# Revit family: WCPan-FloorMounted-65cm-(SpecialNeeds)-Vitra-ConformaSeries_5817B003-0087
name_source: partatom
category: Plumbing Fixtures
revit_build: Autodesk Revit 2017 (Build: 20160225_1515(x64)
units: mm (PartAtom-declared; Revit-internal decimal feet)

## family parameters
Cut with Voids When Loaded = No
Host = Face
OmniClass Number = 23.45.05.21.11
OmniClass Title = Water Closets
Part Type = Normal
Room Calculation Point = No
Round Connector Dimension = Use Diameter
Shared = Yes

## types (2) — shared parameters
BIMobject category = Sanitary - Toilets
CW Connection = Yes
Color = White
Default Elevation = 450 mm  [stored 1.47638 ft]
Description = VitrA Conforma Special Needs Wc Pan
Design country = Turkey
HW Connection = No
IFC Classification = Sanitary Terminal
Main Material = Ceramic
Manufacturer = Vitra
Manufacturer name = Vitra
Masterformat 2014 Code = 22 45 26
Masterformat 2014 Description = Sanitary Facilities
MountingType = Floor Mounted
NBS Referans Code = 35-65-90
NBS Referans Description = Toilet Systems
Nominal Depth (mm) = 650 mm  [stored 2.13255 ft]
Nominal Height (mm) = 450 mm  [stored 1.47638 ft]
Nominal Width (mm) = 355 mm
OmniClass Code = 23-31 19 00
OmniClass Description = Toilets
Product certification = https://vitraglobal.com
Product data url = https://www.vitra.co.uk
Product family = Conforma
Product group = Special Needs Wc Pan
Secondary Material = Ceramic-White
Technical description = https://www.vitra.co.uk
UNSPSC Code = 301815
UNSPSC Description = Sanitary Ware
URL = https://www.vitra.com.tr
Uniclass 1.4 Code = L7216
Uniclass 1.4 Description = Toilets
Uniclass 2.0 Code = SS-35-65-90
Uniclass 2.0 Description = Toilet Systems
Uniclass 2015 Code = Pr_40_20_93
Uniclass 2015 Name = Urinal and WC fittings
Uniformat II Code = D2010
Uniformat II Description = Sanitary Facilities
Vent Connection = No
Warranty Period (Year) = 10 Years
Waste Connection = Yes
Weight Net (kg) = 36,741
Youtube = https://www.youtube.com
zero-valued in all types: Cost

## per-type parameters (varying)
| type | Article No. (default) | Model | Product SKU |
| WCPan-FloorMounted-65cm-(SpecialNeeds)-Vitra-ConformaSeries_5817B003-0087 | 5817B003-0087 | 5817B003-0087 | 5817B003-0087 |
| WCPan-FloorMounted-65cm-(SpecialNeeds)-Vitra-ConformaSeries_5817B003-7700 | 5817B003-7700 | 5817B003-7700 | 5817B003-7700 |

note: [stored X ft] marks values corroborated as IEEE doubles in the binary element streams (Revit-internal decimal feet)

## geometry (parser evidence)
native form markers: Sweep x3
no freeform markers — native parametric forms only
